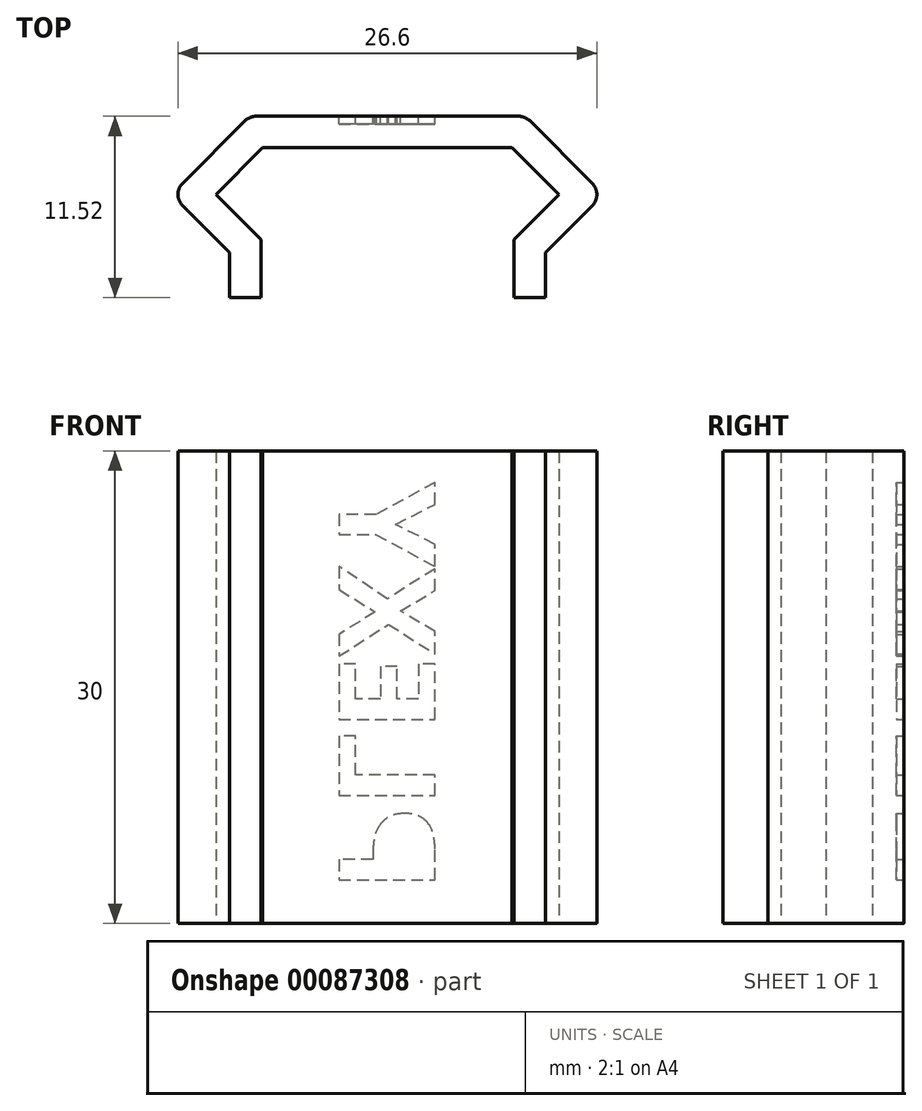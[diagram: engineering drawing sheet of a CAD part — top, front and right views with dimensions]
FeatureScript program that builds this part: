
annotation { "Feature Type Name" : "Feature", "Feature Type Description" : "" }
export const myFeature = defineFeature(function(context is Context, id is Id, definition is map)
    precondition{}
    {
        {
            var Q0;
            Q0=qCreatedBy(makeId("Top.planeOp"),FACE);
            var sketch = newSketch(context, id + "F0", { "sketchPlane" : qUnion([Q0])});
            skLineSegment(sketch, "E0", {"start": v(0, 13.24) * mm, "end": v(0, -16.16) * mm, "construction": true});
            skLineSegment(sketch, "E1", {"start": v(0, -6.21) * mm, "end": v(7.83, -6.21) * mm});
            skLineSegment(sketch, "E2", {"start": v(7.83, -6.21) * mm, "end": v(7.83, -2.43) * mm});
            skLineSegment(sketch, "E3", {"start": v(7.84, -2.43) * mm, "end": v(10.6, 0.34) * mm});
            skLineSegment(sketch, "E4", {"start": v(7.83, 3.1) * mm, "end": v(10.6, 0.34) * mm});
            skLineSegment(sketch, "E5", {"start": v(7.83, 3.1) * mm, "end": v(0, 3.1) * mm});
            skLineSegment(sketch, "E6.MirrorCS", {"start": v(-7.83, 3.1) * mm, "end": v(0, 3.1) * mm});
            skLineSegment(sketch, "E7.MirrorCS", {"start": v(-7.83, 3.1) * mm, "end": v(-10.6, 0.34) * mm});
            skLineSegment(sketch, "E8.MirrorCS", {"start": v(-7.84, -2.43) * mm, "end": v(-10.6, 0.34) * mm});
            skLineSegment(sketch, "E9.MirrorCS", {"start": v(-7.83, -6.21) * mm, "end": v(-7.83, -2.43) * mm});
            skLineSegment(sketch, "E10.MirrorCS", {"start": v(0, -6.21) * mm, "end": v(-7.83, -6.21) * mm});
            skSolve(sketch);
        }
        {
            var Q0;
            Q0=qCreatedBy(makeId("Top.planeOp"),FACE);
            cPlane(context, id + "F1", {"entities" : qUnion([Q0]), "cplaneType" : CPlaneType.OFFSET, "offset" : 10 * mm, "width" : 150 * mm, "height" : 150 * mm});
        }
        {
            var Q0;
            Q0=qCreatedBy(id+"F1.planeOp",FACE);
            var sketch = newSketch(context, id + "F2", { "sketchPlane" : qUnion([Q0])});
            skLineSegment(sketch, "E11.0", {"start": v(-7.83, 3.1) * mm, "end": v(0, 3.1) * mm});
            skLineSegment(sketch, "E12.0", {"start": v(-7.83, 3.1) * mm, "end": v(-10.6, 0.34) * mm});
            skLineSegment(sketch, "E13.0", {"start": v(-7.84, -2.43) * mm, "end": v(-10.6, 0.34) * mm});
            skLineSegment(sketch, "E14.0", {"start": v(-7.83, -6.21) * mm, "end": v(-7.83, -2.43) * mm});
            skLineSegment(sketch, "E15.0", {"start": v(0, -6.21) * mm, "end": v(-7.83, -6.21) * mm});
            skLineSegment(sketch, "E16.0", {"start": v(0, -6.21) * mm, "end": v(7.83, -6.21) * mm});
            skLineSegment(sketch, "E17.0", {"start": v(7.83, -6.21) * mm, "end": v(7.83, -2.43) * mm});
            skLineSegment(sketch, "E18.0", {"start": v(7.84, -2.43) * mm, "end": v(10.6, 0.34) * mm});
            skLineSegment(sketch, "E19.0", {"start": v(7.83, 3.1) * mm, "end": v(10.6, 0.34) * mm});
            skLineSegment(sketch, "E20.0", {"start": v(7.83, 3.1) * mm, "end": v(0, 3.1) * mm});
            skLineSegment(sketch, "E21.0", {"start": v(8.04, -6.21) * mm, "end": v(8.04, -2.52) * mm});
            skLineSegment(sketch, "E21.1", {"start": v(8.04, -2.52) * mm, "end": v(10.89, 0.34) * mm});
            skLineSegment(sketch, "E21.2", {"start": v(7.92, 3.3) * mm, "end": v(10.89, 0.34) * mm});
            skLineSegment(sketch, "E21.3", {"start": v(7.92, 3.3) * mm, "end": v(0, 3.3) * mm});
            skLineSegment(sketch, "E21.4", {"start": v(-8.04, -6.21) * mm, "end": v(-8.04, -2.52) * mm});
            skLineSegment(sketch, "E21.5", {"start": v(-8.04, -2.52) * mm, "end": v(-10.89, 0.34) * mm});
            skLineSegment(sketch, "E21.6", {"start": v(-7.92, 3.3) * mm, "end": v(-10.89, 0.34) * mm});
            skLineSegment(sketch, "E21.7", {"start": v(-7.92, 3.3) * mm, "end": v(0, 3.3) * mm});
            skLineSegment(sketch, "E22.0", {"start": v(10.04, -6.21) * mm, "end": v(10.04, -3.34) * mm});
            skLineSegment(sketch, "E22.1", {"start": v(10.04, -3.34) * mm, "end": v(13.72, 0.34) * mm});
            skLineSegment(sketch, "E22.2", {"start": v(8.75, 5.3) * mm, "end": v(13.72, 0.34) * mm});
            skLineSegment(sketch, "E22.3", {"start": v(8.75, 5.3) * mm, "end": v(0, 5.3) * mm});
            skLineSegment(sketch, "E22.4", {"start": v(-10.04, -6.21) * mm, "end": v(-10.04, -3.34) * mm});
            skLineSegment(sketch, "E22.5", {"start": v(-10.04, -3.34) * mm, "end": v(-13.72, 0.34) * mm});
            skLineSegment(sketch, "E22.6", {"start": v(-8.75, 5.3) * mm, "end": v(-13.72, 0.34) * mm});
            skLineSegment(sketch, "E22.7", {"start": v(-8.75, 5.3) * mm, "end": v(0, 5.3) * mm});
            skLineSegment(sketch, "E23", {"start": v(-10.04, -6.21) * mm, "end": v(-8.04, -6.21) * mm});
            skLineSegment(sketch, "E24", {"start": v(8.04, -6.21) * mm, "end": v(10.04, -6.21) * mm});
            skSolve(sketch);
        }
        {
            var Q0;
            Q0=makeQuery(id+"F2.imprint","IMPRINT",FACE,{"disambiguationData":[TD([[makeQuery(id+"F2.imprint","IMPRINT",EDGE,{"derivedFrom":sQuery(id+"F2.wireOp",EDGE,"E21.0")}),-1.0]])]});
            extrude(context, id + "F3", {"entities" : qUnion([Q0]), "depth" : 30 * mm});
        }
        {
            var Q0;
            Q0=makeQuery(id+"F3.opExtrude","SWEPT_FACE",FACE,{"disambiguationData":[OSD([sQuery(id+"F2.wireOp",EDGE,"E22.3"),sQuery(id+"F2.wireOp",EDGE,"E22.7")])]});
            var sketch = newSketch(context, id + "F4", { "sketchPlane" : qUnion([Q0])});
            skText(sketch, "E25", { "text": "PLEXY", "fontName": "OpenSans-Bold.ttf"});
            skPoint(sketch, "E26", {"position": v(0, 25) * mm});
            skPoint(sketch, "E27.positionSnap0", {"position": v(0, 10) * mm});
            skPoint(sketch, "E27.positionSnap1", {"position": v(-8.75, 25) * mm});
            const initialGuessF4  = {"E25": [0.00308, 0.012, 0, 1, 0.00615]};
            skSetInitialGuess(sketch, initialGuessF4);
            skSolve(sketch);
        }
        {
            var Q0;
            Q0 = qSketchRegion(id + "F4", true);
            var Q1;
            Q1=makeQuery(id+"F4.imprint","IMPRINT",FACE,{"disambiguationData":[TD([[makeQuery(id+"F4.imprint","IMPRINT",EDGE,{"derivedFrom":sQuery(id+"F4.wireOp",EDGE,"E25.sketch_text.stroke-0")}),1.0]])]});
            extrude(context, id + "F5", {"entities" : qUnion([Q0, Q1]), "operationType" : NewBodyOperationType.REMOVE, "oppositeDirection" : true, "depth" : 0.5 * mm});
        }
        {
            var Q0;
            Q0=makeQuery(id+"F3.opExtrude","SWEPT_EDGE",EDGE,{"disambiguationData":[OSD([sQuery(id+"F2.wireOp",EDGE,"E22.5"),sQuery(id+"F2.wireOp",EDGE,"E22.6")])]});
            var Q1;
            Q1=makeQuery(id+"F3.opExtrude","SWEPT_EDGE",EDGE,{"disambiguationData":[OSD([sQuery(id+"F2.wireOp",EDGE,"E22.6"),sQuery(id+"F2.wireOp",EDGE,"E22.7")])]});
            var Q2;
            Q2=makeQuery(id+"F3.opExtrude","SWEPT_EDGE",EDGE,{"disambiguationData":[OSD([sQuery(id+"F2.wireOp",EDGE,"E22.2"),sQuery(id+"F2.wireOp",EDGE,"E22.3")])]});
            var Q3;
            Q3=makeQuery(id+"F3.opExtrude","SWEPT_EDGE",EDGE,{"disambiguationData":[OSD([sQuery(id+"F2.wireOp",EDGE,"E22.1"),sQuery(id+"F2.wireOp",EDGE,"E22.2")])]});
            fillet(context, id + "F6", {"entities" : qUnion([Q0, Q1, Q2, Q3]), "radius" : 1 * mm, "tangentPropagation" : true, "allowEdgeOverflow" : false});
        }
    });
